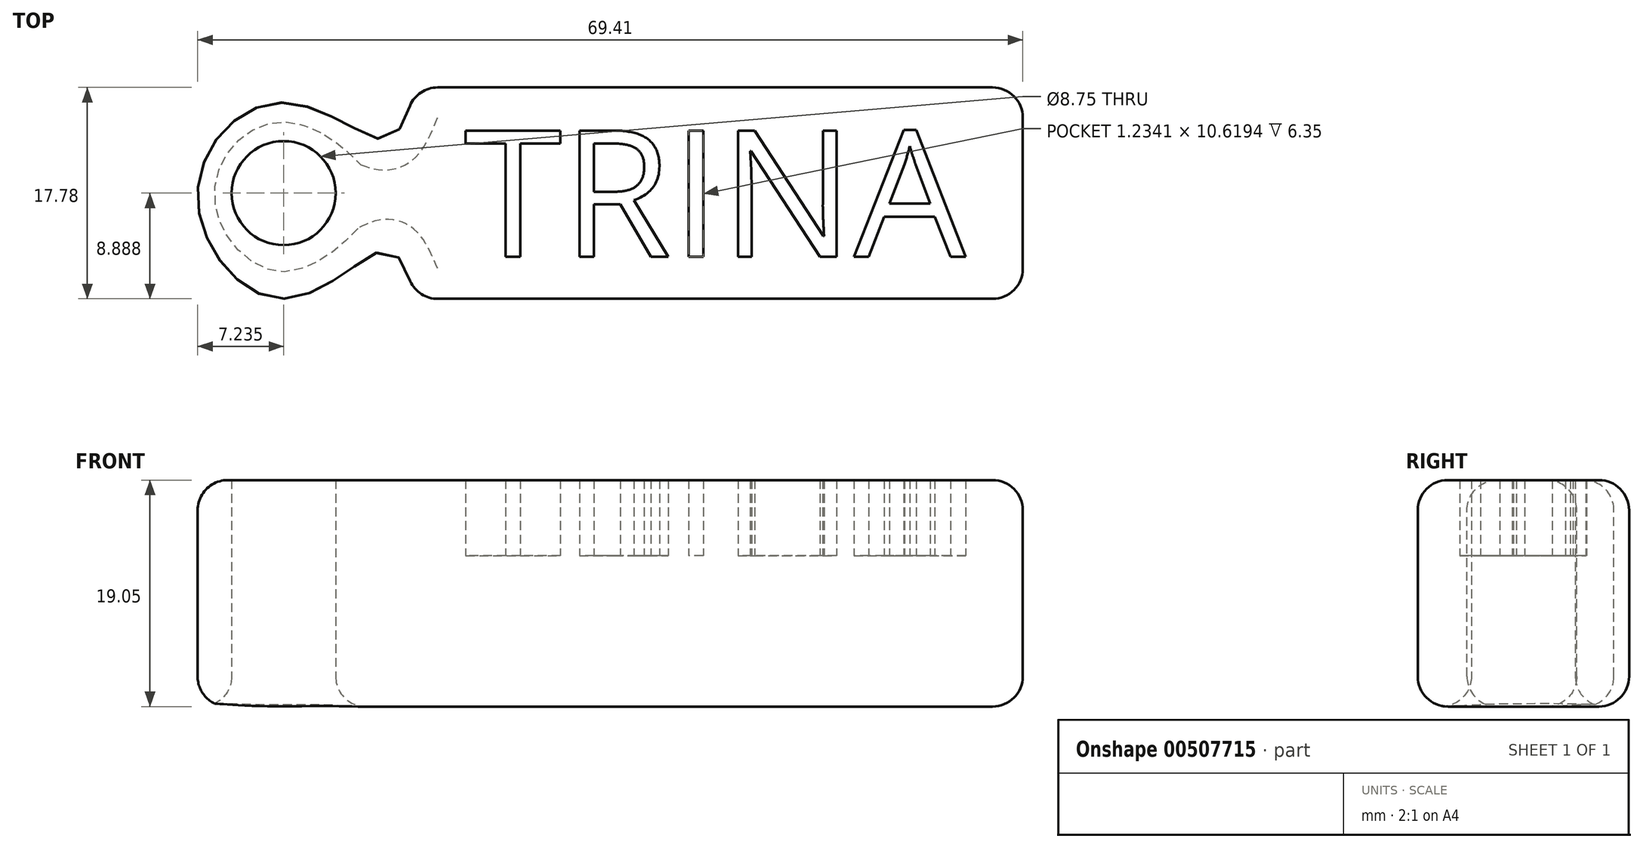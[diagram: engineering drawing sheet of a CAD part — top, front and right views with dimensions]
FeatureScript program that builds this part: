
annotation { "Feature Type Name" : "Feature", "Feature Type Description" : "" }
export const myFeature = defineFeature(function(context is Context, id is Id, definition is map)
    precondition{}
    {
        {
            var Q0;
            Q0=qCreatedBy(makeId("Top.planeOp"),FACE);
            var sketch = newSketch(context, id + "F0", { "sketchPlane" : qUnion([Q0])});
            skLineSegment(sketch, "E0.bottom", {"start": v(-7.03, -3.23) * mm, "end": v(-55.3, -3.23) * mm});
            skLineSegment(sketch, "E0.top", {"start": v(-7.03, 14.55) * mm, "end": v(-55.3, 14.55) * mm});
            skLineSegment(sketch, "E0.left", {"start": v(-4.5, -0.7) * mm, "end": v(-4.5, 12) * mm});
            skLineSegment(sketch, "E0.right", {"start": v(-55.3, -3.23) * mm, "end": v(-55.3, 14.55) * mm});
            skPoint(sketch, "E0.middle", {"position": v(-29.9, 5.66) * mm});
            skText(sketch, "E1", { "text": "TRINA", "fontName": "OpenSans-Regular.ttf"});
            skFitSpline(sketch, "E2", {"points": [v(-55.3, -3.23) * mm, v(-58.1, 0.9) * mm, v(-66.72, -3.23) * mm, v(-73.9, 5.66) * mm, v(-66.72, 13.28) * mm, v(-58.02, 10.16) * mm, v(-55.3, 14.55) * mm], "startDerivative": vector(-30.74, 57.52) * mm, "endDerivative": vector(28.96, 50.49) * mm});
            skCircle(sketch, "E3", {"center": v(-66.67, 5.66) * mm, "radius": 4.37 * mm});
            skPoint(sketch, "E4.visualSharp", {"position": v(-4.5, 14.55) * mm});
            skArc(sketch, "E4.filletArc", {"start": v(-4.5, 12) * mm, "mid": v(-5.24, 13.8) * mm, "end": v(-7.03, 14.55) * mm});
            skPoint(sketch, "E5.visualSharp", {"position": v(-4.5, -3.23) * mm});
            skArc(sketch, "E5.filletArc", {"start": v(-7.03, -3.23) * mm, "mid": v(-5.24, -2.49) * mm, "end": v(-4.5, -0.7) * mm});
            const initialGuessF0  = {"E1": [-0.05148, 0.0003, 1, 0, 0.01071]};
            skSetInitialGuess(sketch, initialGuessF0);
            skSolve(sketch);
        }
        {
            var Q0;
            Q0=makeQuery(id+"F0.imprint","IMPRINT",FACE,{"disambiguationData":[TD([[makeQuery(id+"F0.imprint","IMPRINT",EDGE,{"derivedFrom":sQuery(id+"F0.wireOp",EDGE,"E1.sketch_text.stroke-0")}),-1.0]])]});
            var Q1;
            Q1=makeQuery(id+"F0.imprint","IMPRINT",FACE,{"disambiguationData":[TD([[makeQuery(id+"F0.imprint","IMPRINT",EDGE,{"derivedFrom":sQuery(id+"F0.wireOp",EDGE,"E1.sketch_text.stroke-8")}),-1.0]])]});
            var Q2;
            Q2=makeQuery(id+"F0.imprint","IMPRINT",FACE,{"disambiguationData":[TD([[makeQuery(id+"F0.imprint","IMPRINT",EDGE,{"derivedFrom":sQuery(id+"F0.wireOp",EDGE,"E1.sketch_text.stroke-26")}),-1.0]])]});
            var Q3;
            Q3=makeQuery(id+"F0.imprint","IMPRINT",FACE,{"disambiguationData":[TD([[makeQuery(id+"F0.imprint","IMPRINT",EDGE,{"derivedFrom":sQuery(id+"F0.wireOp",EDGE,"E1.sketch_text.stroke-30")}),-1.0]])]});
            var Q4;
            Q4=makeQuery(id+"F0.imprint","IMPRINT",FACE,{"disambiguationData":[TD([[makeQuery(id+"F0.imprint","IMPRINT",EDGE,{"derivedFrom":sQuery(id+"F0.wireOp",EDGE,"E1.sketch_text.stroke-45")}),-1.0]])]});
            extrude(context, id + "F1", {"entities" : qUnion([Q0, Q1, Q2, Q3, Q4]), "depth" : 12.7 * mm});
        }
        {
            var Q0;
            Q0=makeQuery(id+"F0.imprint","IMPRINT",FACE,{"disambiguationData":[TD([[makeQuery(id+"F0.imprint","IMPRINT",EDGE,{"derivedFrom":sQuery(id+"F0.wireOp",EDGE,"E0.bottom")}),-1.0]])]});
            var Q1;
            Q1=makeQuery(id+"F0.imprint","IMPRINT",FACE,{"disambiguationData":[TD([[makeQuery(id+"F0.imprint","IMPRINT",EDGE,{"derivedFrom":sQuery(id+"F0.wireOp",EDGE,"E1.sketch_text.stroke-19")}),1.0]])]});
            var Q2;
            Q2=makeQuery(id+"F0.imprint","IMPRINT",FACE,{"disambiguationData":[TD([[makeQuery(id+"F0.imprint","IMPRINT",EDGE,{"derivedFrom":sQuery(id+"F0.wireOp",EDGE,"E1.sketch_text.stroke-53")}),1.0]])]});
            extrude(context, id + "F2", {"entities" : qUnion([Q0, Q1, Q2]), "operationType" : NewBodyOperationType.ADD, "depth" : 19.05 * mm});
        }
        {
            var Q0;
            Q0=makeQuery(id+"F0.imprint","IMPRINT",FACE,{"disambiguationData":[TD([[makeQuery(id+"F0.imprint","IMPRINT",EDGE,{"derivedFrom":sQuery(id+"F0.wireOp",EDGE,"E0.right")}),1.0]])]});
            extrude(context, id + "F3", {"entities" : qUnion([Q0]), "operationType" : NewBodyOperationType.ADD, "depth" : 19.05 * mm, "offsetDistance" : 25.4 * mm});
        }
        {
            var Q0;
            {var subQ0=sQuery(id+"F0.wireOp",EDGE,"E2");var subQ1=sQuery(id+"F0.wireOp",EDGE,"E0.right");var subQ2=sQuery(id+"F0.wireOp",EDGE,"E0.top");Q0=makeQuery(id+"F3.boolean.opBoolean","MERGE",EDGE,{"derivedFrom":[makeQuery(id+"F2.opExtrude","SWEPT_EDGE",EDGE,{"disambiguationData":[OSD([subQ2,subQ1,subQ0])]}),makeQuery(id+"F3.opExtrude","SWEPT_EDGE",EDGE,{"disambiguationData":[OSD([subQ2,subQ1,subQ0])]})]});}
            fillet(context, id + "F4", {"entities" : qUnion([Q0]), "radius" : 2.54 * mm, "tangentPropagation" : true, "allowEdgeOverflow" : false});
        }
        {
            var Q0;
            {var subQ0=sQuery(id+"F0.wireOp",EDGE,"E2");var subQ1=sQuery(id+"F0.wireOp",EDGE,"E0.right");var subQ2=sQuery(id+"F0.wireOp",EDGE,"E0.bottom");Q0=makeQuery(id+"F3.boolean.opBoolean","MERGE",EDGE,{"derivedFrom":[makeQuery(id+"F2.opExtrude","SWEPT_EDGE",EDGE,{"disambiguationData":[OSD([subQ2,subQ1,subQ0])]}),makeQuery(id+"F3.opExtrude","SWEPT_EDGE",EDGE,{"disambiguationData":[OSD([subQ2,subQ1,subQ0])]})]});}
            fillet(context, id + "F5", {"entities" : qUnion([Q0]), "radius" : 2.54 * mm, "tangentPropagation" : true, "allowEdgeOverflow" : false});
        }
        {
            var Q0;
            Q0=makeQuery(id+"F2.opExtrude","CAP_EDGE",EDGE,{"disambiguationData":[OSD([sQuery(id+"F0.wireOp",EDGE,"E0.bottom")])],"isStart":false});
            var Q1;
            {var subQ0=sQuery(id+"F0.wireOp",EDGE,"E0.right");var subQ1=sQuery(id+"F0.wireOp",EDGE,"E1.sketch_text.stroke-57");var subQ2=sQuery(id+"F0.wireOp",EDGE,"E1.sketch_text.stroke-56");var subQ3=sQuery(id+"F0.wireOp",EDGE,"E1.sketch_text.stroke-55");var subQ4=sQuery(id+"F0.wireOp",EDGE,"E1.sketch_text.stroke-54");var subQ5=sQuery(id+"F0.wireOp",EDGE,"E1.sketch_text.stroke-53");var subQ6=sQuery(id+"F0.wireOp",EDGE,"E1.sketch_text.stroke-25");var subQ7=sQuery(id+"F0.wireOp",EDGE,"E1.sketch_text.stroke-24");var subQ8=sQuery(id+"F0.wireOp",EDGE,"E1.sketch_text.stroke-23");var subQ9=sQuery(id+"F0.wireOp",EDGE,"E1.sketch_text.stroke-22");var subQ10=sQuery(id+"F0.wireOp",EDGE,"E1.sketch_text.stroke-21");var subQ11=sQuery(id+"F0.wireOp",EDGE,"E1.sketch_text.stroke-20");var subQ12=sQuery(id+"F0.wireOp",EDGE,"E1.sketch_text.stroke-19");var subQ13=sQuery(id+"F0.wireOp",EDGE,"E1.sketch_text.stroke-52");var subQ14=sQuery(id+"F0.wireOp",EDGE,"E1.sketch_text.stroke-51");var subQ15=sQuery(id+"F0.wireOp",EDGE,"E1.sketch_text.stroke-50");var subQ16=sQuery(id+"F0.wireOp",EDGE,"E1.sketch_text.stroke-49");var subQ17=sQuery(id+"F0.wireOp",EDGE,"E1.sketch_text.stroke-48");var subQ18=sQuery(id+"F0.wireOp",EDGE,"E1.sketch_text.stroke-47");var subQ19=sQuery(id+"F0.wireOp",EDGE,"E1.sketch_text.stroke-46");var subQ20=sQuery(id+"F0.wireOp",EDGE,"E1.sketch_text.stroke-45");var subQ21=sQuery(id+"F0.wireOp",EDGE,"E1.sketch_text.stroke-44");var subQ22=sQuery(id+"F0.wireOp",EDGE,"E1.sketch_text.stroke-43");var subQ23=sQuery(id+"F0.wireOp",EDGE,"E1.sketch_text.stroke-42");var subQ24=sQuery(id+"F0.wireOp",EDGE,"E1.sketch_text.stroke-41");var subQ25=sQuery(id+"F0.wireOp",EDGE,"E1.sketch_text.stroke-40");var subQ26=sQuery(id+"F0.wireOp",EDGE,"E1.sketch_text.stroke-39");var subQ27=sQuery(id+"F0.wireOp",EDGE,"E1.sketch_text.stroke-38");var subQ28=sQuery(id+"F0.wireOp",EDGE,"E1.sketch_text.stroke-37");var subQ29=sQuery(id+"F0.wireOp",EDGE,"E1.sketch_text.stroke-36");var subQ30=sQuery(id+"F0.wireOp",EDGE,"E1.sketch_text.stroke-35");var subQ31=sQuery(id+"F0.wireOp",EDGE,"E1.sketch_text.stroke-34");var subQ32=sQuery(id+"F0.wireOp",EDGE,"E1.sketch_text.stroke-33");var subQ33=sQuery(id+"F0.wireOp",EDGE,"E1.sketch_text.stroke-32");var subQ34=sQuery(id+"F0.wireOp",EDGE,"E1.sketch_text.stroke-31");var subQ35=sQuery(id+"F0.wireOp",EDGE,"E1.sketch_text.stroke-30");var subQ36=sQuery(id+"F0.wireOp",EDGE,"E1.sketch_text.stroke-29");var subQ37=sQuery(id+"F0.wireOp",EDGE,"E1.sketch_text.stroke-28");var subQ38=sQuery(id+"F0.wireOp",EDGE,"E1.sketch_text.stroke-27");var subQ39=sQuery(id+"F0.wireOp",EDGE,"E1.sketch_text.stroke-26");var subQ40=sQuery(id+"F0.wireOp",EDGE,"E1.sketch_text.stroke-18");var subQ41=sQuery(id+"F0.wireOp",EDGE,"E1.sketch_text.stroke-17");var subQ42=sQuery(id+"F0.wireOp",EDGE,"E1.sketch_text.stroke-16");var subQ43=sQuery(id+"F0.wireOp",EDGE,"E1.sketch_text.stroke-15");var subQ44=sQuery(id+"F0.wireOp",EDGE,"E1.sketch_text.stroke-14");var subQ45=sQuery(id+"F0.wireOp",EDGE,"E1.sketch_text.stroke-13");var subQ46=sQuery(id+"F0.wireOp",EDGE,"E1.sketch_text.stroke-12");var subQ47=sQuery(id+"F0.wireOp",EDGE,"E1.sketch_text.stroke-11");var subQ48=sQuery(id+"F0.wireOp",EDGE,"E1.sketch_text.stroke-10");var subQ49=sQuery(id+"F0.wireOp",EDGE,"E1.sketch_text.stroke-9");var subQ50=sQuery(id+"F0.wireOp",EDGE,"E1.sketch_text.stroke-8");var subQ51=sQuery(id+"F0.wireOp",EDGE,"E1.sketch_text.stroke-7");var subQ52=sQuery(id+"F0.wireOp",EDGE,"E1.sketch_text.stroke-6");var subQ53=sQuery(id+"F0.wireOp",EDGE,"E1.sketch_text.stroke-5");var subQ54=sQuery(id+"F0.wireOp",EDGE,"E1.sketch_text.stroke-4");var subQ55=sQuery(id+"F0.wireOp",EDGE,"E1.sketch_text.stroke-3");var subQ56=sQuery(id+"F0.wireOp",EDGE,"E1.sketch_text.stroke-2");var subQ57=sQuery(id+"F0.wireOp",EDGE,"E1.sketch_text.stroke-1");var subQ58=sQuery(id+"F0.wireOp",EDGE,"E1.sketch_text.stroke-0");Q1=makeQuery(id+"F3.boolean.opBoolean","MERGE",FACE,{"derivedFrom":[makeQuery(id+"F2.boolean.opBoolean","MERGE",FACE,{"derivedFrom":[makeQuery(id+"F1.opExtrude","CAP_FACE",FACE,{"disambiguationData":[OSD([subQ58,subQ57,subQ56,subQ55,subQ54,subQ53,subQ52,subQ51])],"isStart":true}),makeQuery(id+"F1.opExtrude","CAP_FACE",FACE,{"disambiguationData":[OSD([subQ50,subQ49,subQ48,subQ47,subQ46,subQ45,subQ44,subQ43,subQ42,subQ41,subQ40,subQ12,subQ11,subQ10,subQ9,subQ8,subQ7,subQ6])],"isStart":true}),makeQuery(id+"F1.opExtrude","CAP_FACE",FACE,{"disambiguationData":[OSD([subQ39,subQ38,subQ37,subQ36])],"isStart":true}),makeQuery(id+"F1.opExtrude","CAP_FACE",FACE,{"disambiguationData":[OSD([subQ35,subQ34,subQ33,subQ32,subQ31,subQ30,subQ29,subQ28,subQ27,subQ26,subQ25,subQ24,subQ23,subQ22,subQ21])],"isStart":true}),makeQuery(id+"F1.opExtrude","CAP_FACE",FACE,{"disambiguationData":[OSD([subQ20,subQ19,subQ18,subQ17,subQ16,subQ15,subQ14,subQ13,subQ5,subQ4,subQ3,subQ2,subQ1])],"isStart":true}),makeQuery(id+"F2.opExtrude","CAP_FACE",FACE,{"disambiguationData":[OSD([sQuery(id+"F0.wireOp",EDGE,"E0.bottom"),sQuery(id+"F0.wireOp",EDGE,"E0.top"),sQuery(id+"F0.wireOp",EDGE,"E0.left"),subQ0,subQ58,subQ57,subQ56,subQ55,subQ54,subQ53,subQ52,subQ51,subQ50,subQ49,subQ48,subQ47,subQ46,subQ45,subQ44,subQ43,subQ42,subQ41,subQ40,subQ39,subQ38,subQ37,subQ36,subQ35,subQ34,subQ33,subQ32,subQ31,subQ30,subQ29,subQ28,subQ27,subQ26,subQ25,subQ24,subQ23,subQ22,subQ21,subQ20,subQ19,subQ18,subQ17,subQ16,subQ15,subQ14,subQ13,sQuery(id+"F0.wireOp",EDGE,"E4.filletArc"),sQuery(id+"F0.wireOp",EDGE,"E5.filletArc")])],"isStart":true}),makeQuery(id+"F2.opExtrude","CAP_FACE",FACE,{"disambiguationData":[OSD([subQ12,subQ11,subQ10,subQ9,subQ8,subQ7,subQ6])],"isStart":true}),makeQuery(id+"F2.opExtrude","CAP_FACE",FACE,{"disambiguationData":[OSD([subQ5,subQ4,subQ3,subQ2,subQ1])],"isStart":true})]}),makeQuery(id+"F3.opExtrude","CAP_FACE",FACE,{"disambiguationData":[OSD([subQ0,sQuery(id+"F0.wireOp",EDGE,"E2"),sQuery(id+"F0.wireOp",EDGE,"E3")])],"isStart":true})]});}
            fillet(context, id + "F6", {"entities" : qUnion([Q0, Q1]), "radius" : 2.54 * mm, "tangentPropagation" : true, "allowEdgeOverflow" : false});
        }
    });
